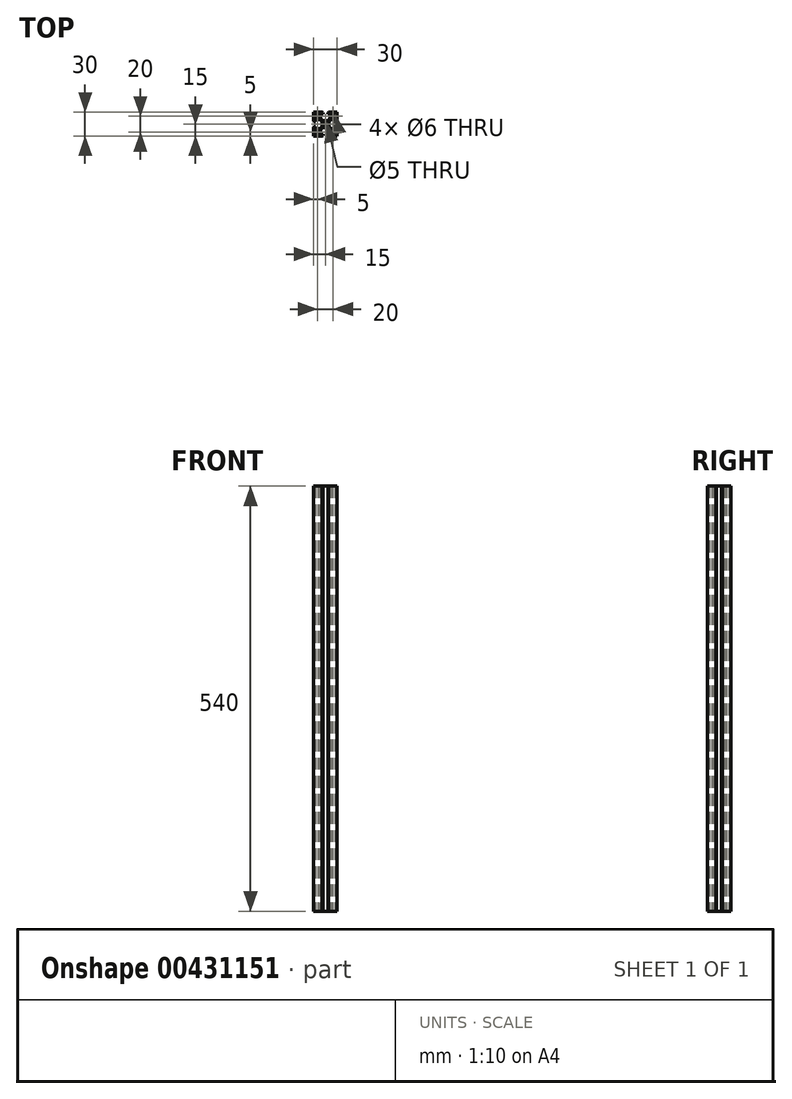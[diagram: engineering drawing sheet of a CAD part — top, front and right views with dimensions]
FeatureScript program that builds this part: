
annotation { "Feature Type Name" : "Feature", "Feature Type Description" : "" }
export const myFeature = defineFeature(function(context is Context, id is Id, definition is map)
    precondition{}
    {
        {
            var Q0;
            Q0=qCreatedBy(makeId("Top.planeOp"),FACE);
            var sketch = newSketch(context, id + "F0", { "sketchPlane" : qUnion([Q0])});
            skLineSegment(sketch, "E0.bottom", {"start": v(15, 15) * mm, "end": v(3.95, 15) * mm});
            skLineSegment(sketch, "E0.top", {"start": v(15, -15) * mm, "end": v(3.95, -15) * mm});
            skLineSegment(sketch, "E0.left", {"start": v(15, 15) * mm, "end": v(15, 3.95) * mm});
            skLineSegment(sketch, "E0.right", {"start": v(-15, 15) * mm, "end": v(-15, 3.95) * mm});
            skPoint(sketch, "E0.middle", {"position": v(0, 0) * mm});
            skLineSegment(sketch, "E1", {"start": v(0, 15) * mm, "end": v(0, -15) * mm, "construction": true});
            skLineSegment(sketch, "E2", {"start": v(-15, 0) * mm, "end": v(15, 0) * mm, "construction": true});
            skCircle(sketch, "E3", {"center": v(-10, 10) * mm, "radius": 3 * mm});
            skCircle(sketch, "E4", {"center": v(0, 0) * mm, "radius": 2.5 * mm});
            skLineSegment(sketch, "E5", {"start": v(0, 15) * mm, "end": v(0, 12.5) * mm, "construction": true});
            skLineSegment(sketch, "E6", {"start": v(-3.15, 14.5) * mm, "end": v(-3.15, 12.5) * mm});
            skLineSegment(sketch, "E7", {"start": v(-3.15, 12.5) * mm, "end": v(-5.1, 12.5) * mm});
            skLineSegment(sketch, "E8", {"start": v(0, 0) * mm, "end": v(-3.44, 0) * mm, "construction": true});
            skLineSegment(sketch, "E9", {"start": v(-5.1, 12.5) * mm, "end": v(-6.18, 9.16) * mm});
            skLineSegment(sketch, "E10", {"start": v(-3.44, 4.5) * mm, "end": v(0, 4.5) * mm});
            skLineSegment(sketch, "E11", {"start": v(3.36, 15) * mm, "end": v(3.36, 11.64) * mm, "construction": true});
            skArc(sketch, "E12", {"start": v(-3.44, 4.5) * mm, "mid": v(-5.13, 6.64) * mm, "end": v(-6.18, 9.16) * mm});
            skLineSegment(sketch, "E13", {"start": v(-3.95, 15) * mm, "end": v(-3.15, 14.5) * mm});
            skLineSegment(sketch, "E14.trimOffspring", {"start": v(-3.95, 15) * mm, "end": v(-5.1, 15) * mm, "construction": true});
            skLineSegment(sketch, "E15", {"start": v(-15, 15) * mm, "end": v(15, -15) * mm, "construction": true});
            skLineSegment(sketch, "E16", {"start": v(15, 15) * mm, "end": v(-15, -15) * mm, "construction": true});
            skArc(sketch, "E17.MirrorCS", {"start": v(-4.5, 3.43) * mm, "mid": v(-6.64, 5.13) * mm, "end": v(-9.16, 6.18) * mm});
            skLineSegment(sketch, "E18.MirrorCS", {"start": v(-4.5, 3.43) * mm, "end": v(-4.5, 0) * mm});
            skLineSegment(sketch, "E19.MirrorCS", {"start": v(-12.5, 5.1) * mm, "end": v(-9.16, 6.18) * mm});
            skLineSegment(sketch, "E20.MirrorCS", {"start": v(-12.5, 3.15) * mm, "end": v(-12.5, 5.1) * mm});
            skLineSegment(sketch, "E21.MirrorCS", {"start": v(-15, 3.95) * mm, "end": v(-14.5, 3.15) * mm});
            skLineSegment(sketch, "E22.MirrorCS", {"start": v(-14.5, 3.15) * mm, "end": v(-12.5, 3.15) * mm});
            skLineSegment(sketch, "E23.MirrorCS", {"start": v(-14.5, -3.15) * mm, "end": v(-12.5, -3.15) * mm});
            skLineSegment(sketch, "E24.MirrorCS", {"start": v(-15, -3.95) * mm, "end": v(-14.5, -3.15) * mm});
            skLineSegment(sketch, "E25.MirrorCS", {"start": v(-12.5, -3.15) * mm, "end": v(-12.5, -5.1) * mm});
            skLineSegment(sketch, "E26.MirrorCS", {"start": v(-12.5, -5.1) * mm, "end": v(-9.16, -6.18) * mm});
            skArc(sketch, "E27.MirrorCS", {"start": v(-4.5, -3.43) * mm, "mid": v(-6.64, -5.13) * mm, "end": v(-9.16, -6.18) * mm});
            skLineSegment(sketch, "E28.MirrorCS", {"start": v(-4.5, -3.43) * mm, "end": v(-4.5, 0) * mm});
            skLineSegment(sketch, "E29.MirrorCS", {"start": v(-3.44, -4.5) * mm, "end": v(0, -4.5) * mm});
            skArc(sketch, "E30.MirrorCS", {"start": v(-3.44, -4.5) * mm, "mid": v(-5.13, -6.64) * mm, "end": v(-6.18, -9.16) * mm});
            skLineSegment(sketch, "E31.MirrorCS", {"start": v(-5.1, -12.5) * mm, "end": v(-6.18, -9.16) * mm});
            skLineSegment(sketch, "E32.MirrorCS", {"start": v(-3.15, -12.5) * mm, "end": v(-5.1, -12.5) * mm});
            skLineSegment(sketch, "E33.MirrorCS", {"start": v(-3.95, -15) * mm, "end": v(-3.15, -14.5) * mm});
            skLineSegment(sketch, "E34.MirrorCS", {"start": v(-3.15, -14.5) * mm, "end": v(-3.15, -12.5) * mm});
            skLineSegment(sketch, "E35.MirrorCS", {"start": v(3.44, -4.5) * mm, "end": v(0, -4.5) * mm});
            skArc(sketch, "E36.MirrorCS", {"start": v(3.44, -4.5) * mm, "mid": v(5.13, -6.64) * mm, "end": v(6.18, -9.16) * mm});
            skLineSegment(sketch, "E37.MirrorCS", {"start": v(5.1, -12.5) * mm, "end": v(6.18, -9.16) * mm});
            skLineSegment(sketch, "E38.MirrorCS", {"start": v(3.15, -12.5) * mm, "end": v(5.1, -12.5) * mm});
            skLineSegment(sketch, "E39.MirrorCS", {"start": v(3.15, -14.5) * mm, "end": v(3.15, -12.5) * mm});
            skLineSegment(sketch, "E40.MirrorCS", {"start": v(3.95, -15) * mm, "end": v(3.15, -14.5) * mm});
            skArc(sketch, "E41.MirrorCS", {"start": v(4.5, -3.43) * mm, "mid": v(6.64, -5.13) * mm, "end": v(9.16, -6.18) * mm});
            skLineSegment(sketch, "E42.MirrorCS", {"start": v(4.5, 3.44) * mm, "end": v(4.5, 0) * mm});
            skLineSegment(sketch, "E43.MirrorCS", {"start": v(4.5, -3.43) * mm, "end": v(4.5, 0) * mm});
            skArc(sketch, "E44.MirrorCS", {"start": v(4.5, 3.44) * mm, "mid": v(6.64, 5.13) * mm, "end": v(9.16, 6.18) * mm});
            skLineSegment(sketch, "E45.MirrorCS", {"start": v(12.5, 5.1) * mm, "end": v(9.16, 6.18) * mm});
            skLineSegment(sketch, "E46.MirrorCS", {"start": v(12.5, -5.1) * mm, "end": v(9.16, -6.18) * mm});
            skLineSegment(sketch, "E47.MirrorCS", {"start": v(12.5, -3.15) * mm, "end": v(12.5, -5.1) * mm});
            skLineSegment(sketch, "E48.MirrorCS", {"start": v(14.5, -3.15) * mm, "end": v(12.5, -3.15) * mm});
            skLineSegment(sketch, "E49.MirrorCS", {"start": v(12.5, 3.15) * mm, "end": v(12.5, 5.1) * mm});
            skLineSegment(sketch, "E50.MirrorCS", {"start": v(14.5, 3.15) * mm, "end": v(12.5, 3.15) * mm});
            skLineSegment(sketch, "E51.MirrorCS", {"start": v(15, 3.95) * mm, "end": v(14.5, 3.15) * mm});
            skLineSegment(sketch, "E52.MirrorCS", {"start": v(15, -3.95) * mm, "end": v(14.5, -3.15) * mm});
            skLineSegment(sketch, "E53.MirrorCS", {"start": v(3.43, 4.5) * mm, "end": v(0, 4.5) * mm});
            skArc(sketch, "E54.MirrorCS", {"start": v(3.43, 4.5) * mm, "mid": v(5.13, 6.64) * mm, "end": v(6.18, 9.16) * mm});
            skLineSegment(sketch, "E55.MirrorCS", {"start": v(5.1, 12.5) * mm, "end": v(6.18, 9.16) * mm});
            skLineSegment(sketch, "E56.MirrorCS", {"start": v(3.15, 12.5) * mm, "end": v(5.1, 12.5) * mm});
            skLineSegment(sketch, "E57.MirrorCS", {"start": v(3.15, 14.5) * mm, "end": v(3.15, 12.5) * mm});
            skLineSegment(sketch, "E58.MirrorCS", {"start": v(3.95, 15) * mm, "end": v(3.15, 14.5) * mm});
            skCircle(sketch, "E59.MirrorC", {"center": v(10, 10) * mm, "radius": 3 * mm});
            skCircle(sketch, "E60.MirrorC", {"center": v(10, -10) * mm, "radius": 3 * mm});
            skCircle(sketch, "E61.MirrorC", {"center": v(-10, -10) * mm, "radius": 3 * mm});
            skLineSegment(sketch, "E62.trimOffspring", {"start": v(-15, -3.95) * mm, "end": v(-15, -15) * mm});
            skPoint(sketch, "E63.orphan", {"position": v(-15, 3.15) * mm});
            skPoint(sketch, "E64.orphan", {"position": v(-15, -3.15) * mm});
            skLineSegment(sketch, "E65.trimOffspring", {"start": v(-3.95, -15) * mm, "end": v(-15, -15) * mm});
            skPoint(sketch, "E66.orphan", {"position": v(-3.15, -15) * mm});
            skPoint(sketch, "E67.orphan", {"position": v(3.15, -15) * mm});
            skLineSegment(sketch, "E68.trimOffspring", {"start": v(15, -3.95) * mm, "end": v(15, -15) * mm});
            skPoint(sketch, "E69.orphan", {"position": v(15, 3.15) * mm});
            skPoint(sketch, "E70.orphan", {"position": v(15, -3.15) * mm});
            skPoint(sketch, "E71.trimOffspring.end.orphan", {"position": v(3.15, 15) * mm});
            skLineSegment(sketch, "E72.trimOffspring", {"start": v(-3.95, 15) * mm, "end": v(-15, 15) * mm});
            skPoint(sketch, "E73.trimOffspring.end.orphan", {"position": v(-3.15, 15) * mm});
            skLineSegment(sketch, "E74", {"start": v(-3.95, 15) * mm, "end": v(3.95, 15) * mm});
            skLineSegment(sketch, "E75", {"start": v(-15, 3.95) * mm, "end": v(-15, -3.95) * mm});
            skLineSegment(sketch, "E76", {"start": v(-3.95, -15) * mm, "end": v(3.95, -15) * mm});
            skLineSegment(sketch, "E77", {"start": v(15, 3.95) * mm, "end": v(15, -3.95) * mm});
            skSolve(sketch);
        }
        {
            var Q0;
            Q0=makeQuery(id+"F0.imprint","IMPRINT",FACE,{"disambiguationData":[TD([[makeQuery(id+"F0.imprint","IMPRINT",EDGE,{"derivedFrom":sQuery(id+"F0.wireOp",EDGE,"E0.bottom")}),1.0]])]});
            extrude(context, id + "F1", {"entities" : qUnion([Q0]), "endBound" : BoundingType.SYMMETRIC, "depth" : 540 * mm});
        }
    });
